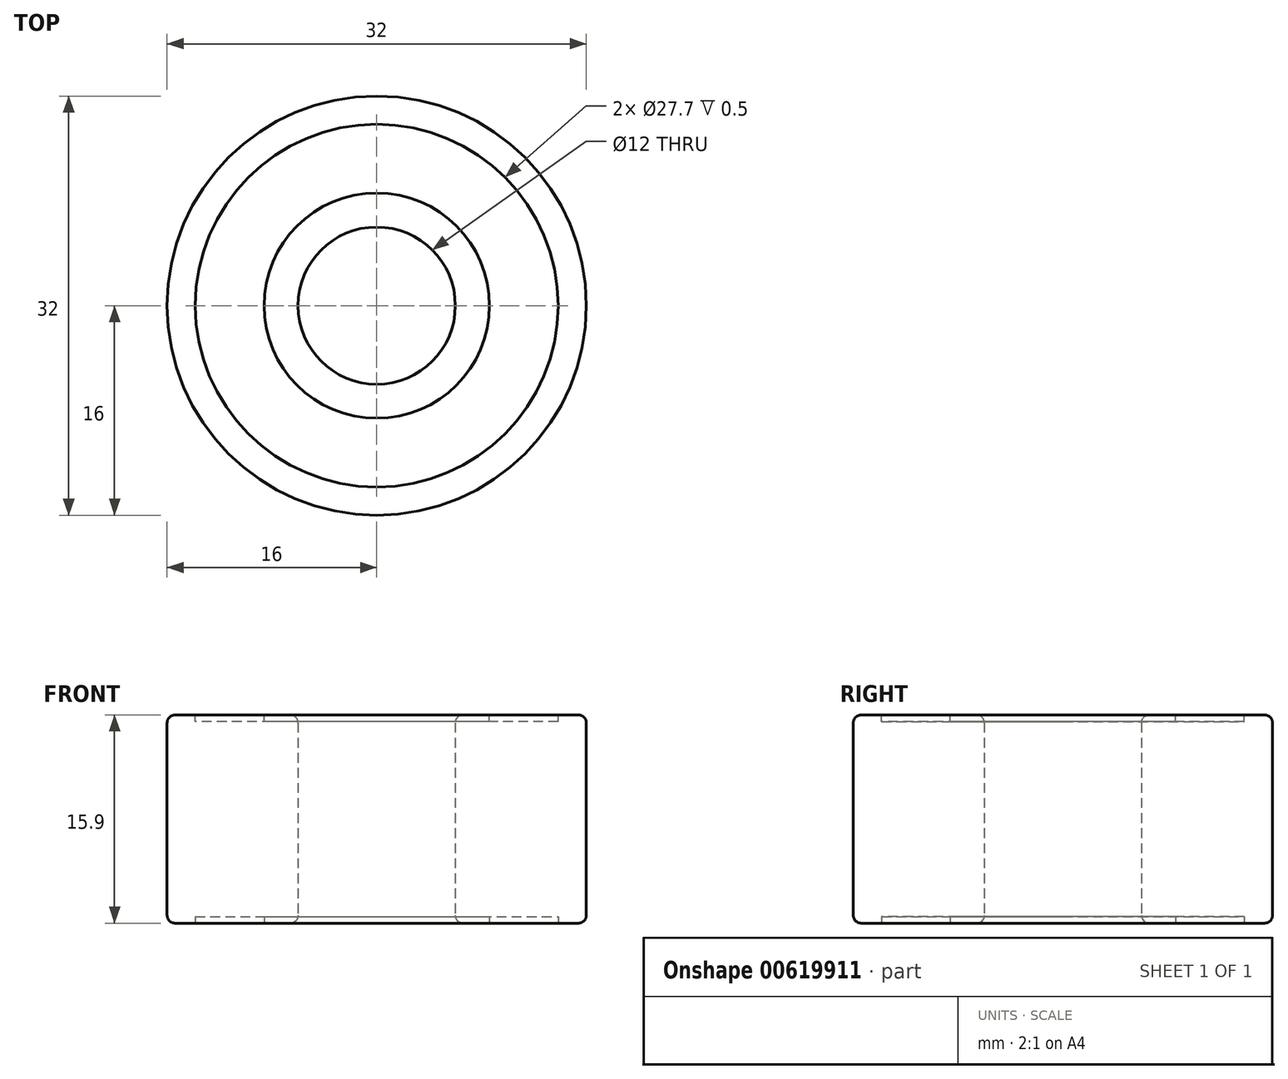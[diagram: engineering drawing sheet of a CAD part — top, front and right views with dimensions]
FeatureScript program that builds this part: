
annotation { "Feature Type Name" : "Feature", "Feature Type Description" : "" }
export const myFeature = defineFeature(function(context is Context, id is Id, definition is map)
    precondition{}
    {
        {
            var Q0;
            Q0=qCreatedBy(makeId("Top.planeOp"),FACE);
            var sketch = newSketch(context, id + "F0", { "sketchPlane" : qUnion([Q0])});
            skCircle(sketch, "E0", {"center": v(0, 0) * mm, "radius": 6 * mm});
            skCircle(sketch, "E1", {"center": v(0, 0) * mm, "radius": 16 * mm});
            skSolve(sketch);
        }
        {
            var Q0;
            Q0 = qSketchRegion(id + "F0", true);
            extrude(context, id + "F1", {"entities" : qUnion([Q0]), "depth" : 15.9 * mm, "offsetDistance" : 25 * mm});
        }
        {
            var Q0;
            Q0=makeQuery(id+"F1.opExtrude","SWEPT_FACE",FACE,{"disambiguationData":[OSD([sQuery(id+"F0.wireOp",EDGE,"E0")])]});
            var Q1;
            Q1=makeQuery(id+"F1.opExtrude","SWEPT_FACE",FACE,{"disambiguationData":[OSD([sQuery(id+"F0.wireOp",EDGE,"E1")])]});
            fillet(context, id + "F2", {"entities" : qUnion([Q0, Q1]), "radius" : .6 * mm, "tangentPropagation" : true, "allowEdgeOverflow" : false});
        }
        {
            var Q0;
            Q0=makeQuery(id+"F1.opExtrude","CAP_FACE",FACE,{"disambiguationData":[OSD([sQuery(id+"F0.wireOp",EDGE,"E0"),sQuery(id+"F0.wireOp",EDGE,"E1")])],"isStart":false});
            var sketch = newSketch(context, id + "F3", { "sketchPlane" : qUnion([Q0])});
            skCircle(sketch, "E2", {"center": v(0, 0) * mm, "radius": 8.6 * mm});
            skCircle(sketch, "E3", {"center": v(0, 0) * mm, "radius": 13.85 * mm});
            skSolve(sketch);
        }
        {
            var Q0;
            Q0 = qSketchRegion(id + "F3", true);
            extrude(context, id + "F4", {"entities" : qUnion([Q0]), "operationType" : NewBodyOperationType.REMOVE, "oppositeDirection" : true, "depth" : .5 * mm, "offsetDistance" : 25 * mm});
        }
        {
            var Q0;
            Q0=makeQuery(id+"F1.opExtrude","CAP_FACE",FACE,{"disambiguationData":[OSD([sQuery(id+"F0.wireOp",EDGE,"E0"),sQuery(id+"F0.wireOp",EDGE,"E1")])],"isStart":true});
            var sketch = newSketch(context, id + "F5", { "sketchPlane" : qUnion([Q0])});
            skCircle(sketch, "E4", {"center": v(0, 0) * mm, "radius": 8.6 * mm});
            skCircle(sketch, "E5", {"center": v(0, 0) * mm, "radius": 13.85 * mm});
            skSolve(sketch);
        }
        {
            var Q0;
            Q0 = qSketchRegion(id + "F5", true);
            extrude(context, id + "F6", {"entities" : qUnion([Q0]), "operationType" : NewBodyOperationType.REMOVE, "oppositeDirection" : true, "depth" : .5 * mm, "offsetDistance" : 25 * mm});
        }
    });
